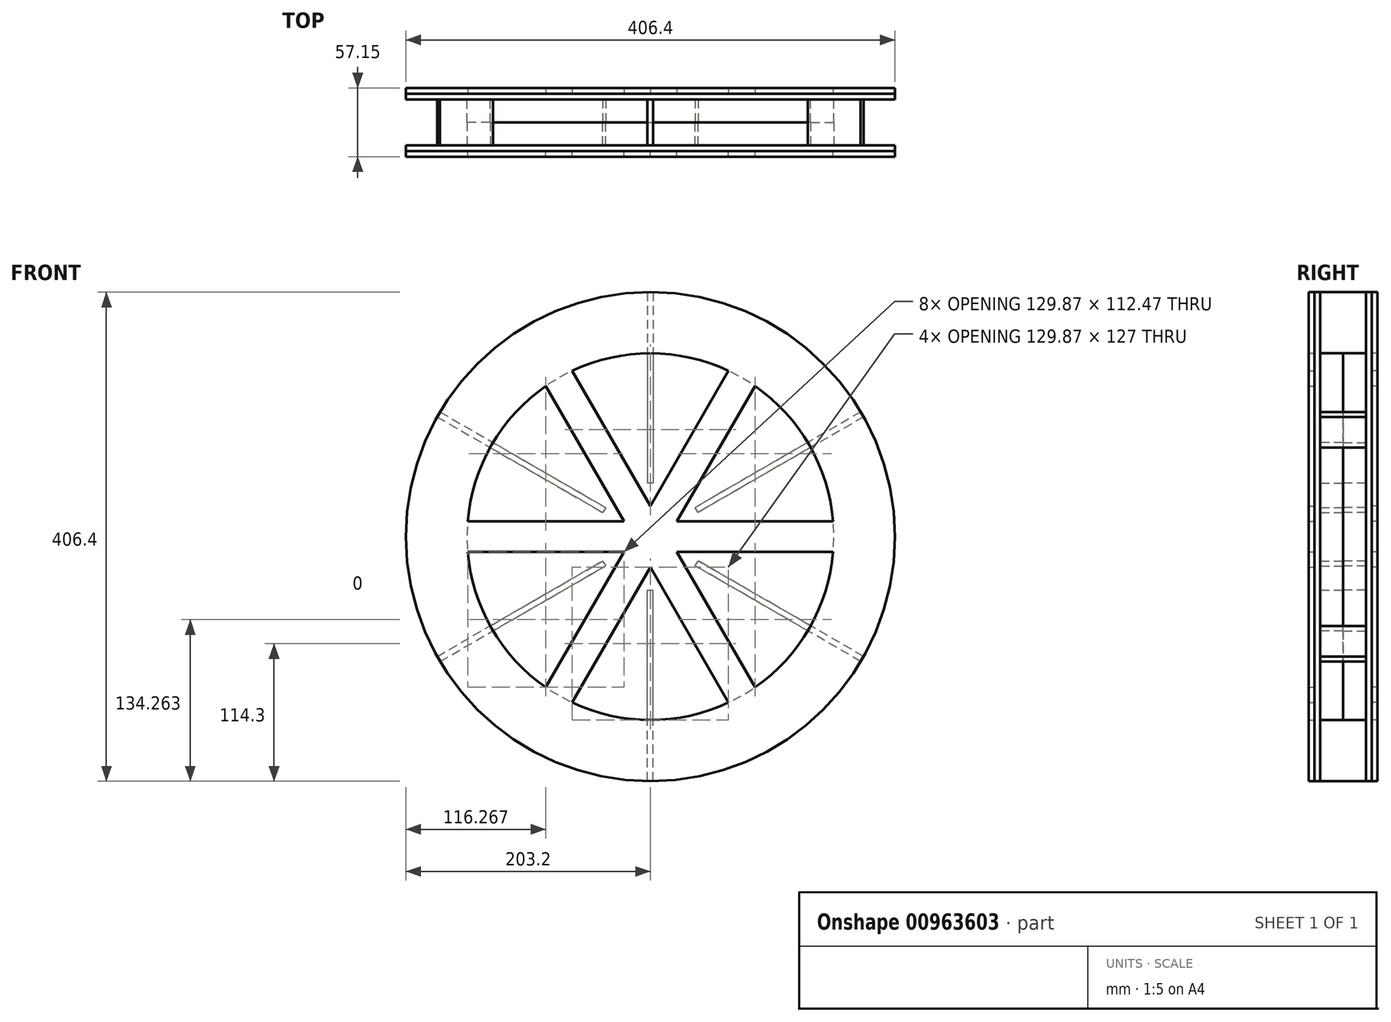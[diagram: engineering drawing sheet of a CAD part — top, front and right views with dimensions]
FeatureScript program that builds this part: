
annotation { "Feature Type Name" : "Feature", "Feature Type Description" : "" }
export const myFeature = defineFeature(function(context is Context, id is Id, definition is map)
    precondition{}
    {
        {
            var Q0;
            Q0=qCreatedBy(makeId("Front.planeOp"),FACE);
            var sketch = newSketch(context, id + "F0", { "sketchPlane" : qUnion([Q0])});
            skCircle(sketch, "E0", {"center": v(0, 0) * mm, "radius": 203.2 * mm});
            skArc(sketch, "E1", {"start": v(-151.87, -12.7) * mm, "mid": v(-131.98, -76.2) * mm, "end": v(-86.93, -125.17) * mm});
            skLineSegment(sketch, "E2.bottom", {"start": v(151.87, 12.7) * mm, "end": v(22, 12.7) * mm});
            skLineSegment(sketch, "E2.top", {"start": v(151.87, -12.7) * mm, "end": v(22, -12.7) * mm});
            skLineSegment(sketch, "E3.left", {"start": v(86.93, 125.17) * mm, "end": v(22, 12.7) * mm});
            skLineSegment(sketch, "E3.right", {"start": v(64.94, 137.87) * mm, "end": v(0, 25.4) * mm});
            skLineSegment(sketch, "E4", {"start": v(0, 0) * mm, "end": v(0, 203.2) * mm, "construction": true});
            skLineSegment(sketch, "E5.MirrorCS", {"start": v(-64.94, 137.87) * mm, "end": v(0, 25.4) * mm});
            skLineSegment(sketch, "E6.MirrorCS", {"start": v(-86.93, 125.17) * mm, "end": v(-22, 12.7) * mm});
            skArc(sketch, "E7.trimOffspring", {"start": v(-86.93, 125.17) * mm, "mid": v(-131.98, 76.2) * mm, "end": v(-151.87, 12.7) * mm});
            skArc(sketch, "E8.trimOffspring", {"start": v(64.94, 137.87) * mm, "mid": v(0, 152.4) * mm, "end": v(-64.94, 137.87) * mm});
            skArc(sketch, "E9.trimOffspring", {"start": v(151.87, 12.7) * mm, "mid": v(131.98, 76.2) * mm, "end": v(86.93, 125.17) * mm});
            skArc(sketch, "E10.trimOffspring", {"start": v(86.93, -125.17) * mm, "mid": v(131.98, -76.2) * mm, "end": v(151.87, -12.7) * mm});
            skArc(sketch, "E11.trimOffspring", {"start": v(-64.94, -137.87) * mm, "mid": v(0, -152.4) * mm, "end": v(64.94, -137.87) * mm});
            skLineSegment(sketch, "E12.trimOffspring", {"start": v(-22, -12.7) * mm, "end": v(-86.93, -125.17) * mm});
            skLineSegment(sketch, "E13.trimOffspring", {"start": v(-22, 12.7) * mm, "end": v(-151.87, 12.7) * mm});
            skLineSegment(sketch, "E14.trimOffspring", {"start": v(0, -25.4) * mm, "end": v(64.94, -137.87) * mm});
            skLineSegment(sketch, "E15.trimOffspring", {"start": v(-22, -12.7) * mm, "end": v(-151.87, -12.7) * mm});
            skLineSegment(sketch, "E16.trimOffspring", {"start": v(22, -12.7) * mm, "end": v(86.93, -125.17) * mm});
            skLineSegment(sketch, "E17.trimOffspring", {"start": v(0, -25.4) * mm, "end": v(-64.94, -137.87) * mm});
            skLineSegment(sketch, "E18", {"start": v(22, 12.7) * mm, "end": v(22, -12.7) * mm, "construction": true});
            skLineSegment(sketch, "E19", {"start": v(22, 12.7) * mm, "end": v(0, 25.4) * mm, "construction": true});
            skLineSegment(sketch, "E20", {"start": v(-22, 12.7) * mm, "end": v(0, 25.4) * mm, "construction": true});
            skSolve(sketch);
        }
        {
            var Q0;
            Q0 = qSketchRegion(id + "F0", true);
            extrude(context, id + "F1", {"entities" : qUnion([Q0]), "depth" : 4.76 * mm, "offsetDistance" : 25.4 * mm});
        }
        {
            var Q0;
            Q0=makeQuery(id+"F1.opExtrude","CAP_FACE",FACE,{"disambiguationData":[OSD([sQuery(id+"F0.wireOp",EDGE,"E0"),sQuery(id+"F0.wireOp",EDGE,"E1"),sQuery(id+"F0.wireOp",EDGE,"E2.bottom"),sQuery(id+"F0.wireOp",EDGE,"E2.top"),sQuery(id+"F0.wireOp",EDGE,"E3.left"),sQuery(id+"F0.wireOp",EDGE,"E3.right"),sQuery(id+"F0.wireOp",EDGE,"E5.MirrorCS"),sQuery(id+"F0.wireOp",EDGE,"E6.MirrorCS"),sQuery(id+"F0.wireOp",EDGE,"E7.trimOffspring"),sQuery(id+"F0.wireOp",EDGE,"E8.trimOffspring"),sQuery(id+"F0.wireOp",EDGE,"E9.trimOffspring"),sQuery(id+"F0.wireOp",EDGE,"E10.trimOffspring"),sQuery(id+"F0.wireOp",EDGE,"E11.trimOffspring"),sQuery(id+"F0.wireOp",EDGE,"E12.trimOffspring"),sQuery(id+"F0.wireOp",EDGE,"E13.trimOffspring"),sQuery(id+"F0.wireOp",EDGE,"E14.trimOffspring"),sQuery(id+"F0.wireOp",EDGE,"E15.trimOffspring"),sQuery(id+"F0.wireOp",EDGE,"E16.trimOffspring"),sQuery(id+"F0.wireOp",EDGE,"E17.trimOffspring")])],"isStart":true});
            var sketch = newSketch(context, id + "F2", { "sketchPlane" : qUnion([Q0])});
            skCircle(sketch, "E21.0", {"center": v(0, 0) * mm, "radius": 203.2 * mm});
            skSolve(sketch);
        }
        {
            var Q0;
            Q0 = qSketchRegion(id + "F2", true);
            extrude(context, id + "F3", {"entities" : qUnion([Q0]), "depth" : 4.76 * mm, "offsetDistance" : 25.4 * mm});
        }
        {
            var Q0;
            Q0=makeQuery(id+"F3.opExtrude","CAP_FACE",FACE,{"disambiguationData":[OSD([sQuery(id+"F2.wireOp",EDGE,"E21.0")])],"isStart":false});
            var sketch = newSketch(context, id + "F4", { "sketchPlane" : qUnion([Q0])});
            skCircle(sketch, "E22", {"center": v(0, 0) * mm, "radius": 152.4 * mm});
            skSolve(sketch);
        }
        {
            var Q0;
            Q0 = qSketchRegion(id + "F4", true);
            extrude(context, id + "F5", {"entities" : qUnion([Q0]), "depth" : 19.05 * mm, "offsetDistance" : 25.4 * mm});
        }
        {
            var Q0;
            Q0=makeQuery(id+"F5.opExtrude","CAP_FACE",FACE,{"disambiguationData":[OSD([sQuery(id+"F4.wireOp",EDGE,"E22")])],"isStart":false});
            var sketch = newSketch(context, id + "F6", { "sketchPlane" : qUnion([Q0])});
            skCircle(sketch, "E23.0", {"center": v(0, 0) * mm, "radius": 203.2 * mm, "construction": true});
            skLineSegment(sketch, "E24.bottom", {"start": v(-2.38, 203.19) * mm, "end": v(2.38, 203.19) * mm});
            skLineSegment(sketch, "E24.top", {"start": v(-2.38, 44.43) * mm, "end": v(2.38, 44.43) * mm});
            skLineSegment(sketch, "E24.left", {"start": v(-2.38, 203.19) * mm, "end": v(-2.38, 44.43) * mm});
            skLineSegment(sketch, "E24.right", {"start": v(2.38, 203.19) * mm, "end": v(2.38, 44.43) * mm});
            skPoint(sketch, "E25", {"position": v(2.38, 152.38) * mm});
            skLineSegment(sketch, "E26.1.0", {"start": v(-174.77, 103.66) * mm, "end": v(-37.29, 24.28) * mm});
            skLineSegment(sketch, "E26.1.1", {"start": v(-177.15, 99.53) * mm, "end": v(-39.67, 20.15) * mm});
            skPoint(sketch, "E26.1.2", {"position": v(-130.78, 78.25) * mm});
            skLineSegment(sketch, "E26.1.3", {"start": v(-39.67, 20.15) * mm, "end": v(-37.29, 24.28) * mm});
            skLineSegment(sketch, "E26.1.4", {"start": v(-177.15, 99.53) * mm, "end": v(-174.77, 103.66) * mm});
            skLineSegment(sketch, "E26.2.0", {"start": v(-177.15, -99.53) * mm, "end": v(-39.67, -20.15) * mm});
            skLineSegment(sketch, "E26.2.1", {"start": v(-174.77, -103.66) * mm, "end": v(-37.29, -24.28) * mm});
            skPoint(sketch, "E26.2.2", {"position": v(-133.16, -74.13) * mm});
            skLineSegment(sketch, "E26.2.3", {"start": v(-37.29, -24.28) * mm, "end": v(-39.67, -20.15) * mm});
            skLineSegment(sketch, "E26.2.4", {"start": v(-174.77, -103.66) * mm, "end": v(-177.15, -99.53) * mm});
            skLineSegment(sketch, "E26.3.0", {"start": v(-2.38, -203.19) * mm, "end": v(-2.38, -44.43) * mm});
            skLineSegment(sketch, "E26.3.1", {"start": v(2.38, -203.19) * mm, "end": v(2.38, -44.43) * mm});
            skPoint(sketch, "E26.3.2", {"position": v(-2.38, -152.38) * mm});
            skLineSegment(sketch, "E26.3.3", {"start": v(2.38, -44.43) * mm, "end": v(-2.38, -44.43) * mm});
            skLineSegment(sketch, "E26.3.4", {"start": v(2.38, -203.19) * mm, "end": v(-2.38, -203.19) * mm});
            skLineSegment(sketch, "E26.4.0", {"start": v(174.77, -103.66) * mm, "end": v(37.29, -24.28) * mm});
            skLineSegment(sketch, "E26.4.1", {"start": v(177.15, -99.53) * mm, "end": v(39.67, -20.15) * mm});
            skPoint(sketch, "E26.4.2", {"position": v(130.78, -78.25) * mm});
            skLineSegment(sketch, "E26.4.3", {"start": v(39.67, -20.15) * mm, "end": v(37.29, -24.28) * mm});
            skLineSegment(sketch, "E26.4.4", {"start": v(177.15, -99.53) * mm, "end": v(174.77, -103.66) * mm});
            skLineSegment(sketch, "E26.5.0", {"start": v(177.15, 99.53) * mm, "end": v(39.67, 20.15) * mm});
            skLineSegment(sketch, "E26.5.1", {"start": v(174.77, 103.66) * mm, "end": v(37.29, 24.28) * mm});
            skPoint(sketch, "E26.5.2", {"position": v(133.16, 74.13) * mm});
            skLineSegment(sketch, "E26.5.3", {"start": v(37.29, 24.28) * mm, "end": v(39.67, 20.15) * mm});
            skLineSegment(sketch, "E26.5.4", {"start": v(174.77, 103.66) * mm, "end": v(177.15, 99.53) * mm});
            skSolve(sketch);
        }
        {
            var Q0;
            Q0 = qSketchRegion(id + "F6", true);
            var Q1;
            Q1=makeQuery(id+"F3.opExtrude","CAP_FACE",FACE,{"disambiguationData":[OSD([sQuery(id+"F2.wireOp",EDGE,"E21.0")])],"isStart":false});
            extrude(context, id + "F7", {"entities" : qUnion([Q0]), "operationType" : NewBodyOperationType.REMOVE, "endBound" : BoundingType.UP_TO_SURFACE, "oppositeDirection" : true, "depth" : 25.4 * mm, "endBoundEntityFace" : qUnion([Q1]), "offsetDistance" : 25.4 * mm});
        }
        {
            var Q0;
            Q0=makeQuery(id+"F5.opExtrude","CAP_FACE",FACE,{"disambiguationData":[OSD([sQuery(id+"F4.wireOp",EDGE,"E22")])],"isStart":false});
            cPlane(context, id + "F8", {"entities" : qUnion([Q0]), "cplaneType" : CPlaneType.OFFSET, "offset" : 0 * mm, "width" : 152.4 * mm, "height" : 152.4 * mm});
        }
        {
            var Q0;
            Q0=makeQuery(id+"F5.opExtrude","SWEPT_BODY",BODY,{"disambiguationData":[OSD([sQuery(id+"F4.wireOp",EDGE,"E22")])]});
            var Q1;
            Q1=makeQuery(id+"F3.opExtrude","SWEPT_BODY",BODY,{"disambiguationData":[OSD([sQuery(id+"F2.wireOp",EDGE,"E21.0")])]});
            var Q2;
            Q2=makeQuery(id+"F1.opExtrude","SWEPT_BODY",BODY,{"disambiguationData":[OSD([sQuery(id+"F0.wireOp",EDGE,"E0"),sQuery(id+"F0.wireOp",EDGE,"E1"),sQuery(id+"F0.wireOp",EDGE,"E2.bottom"),sQuery(id+"F0.wireOp",EDGE,"E2.top"),sQuery(id+"F0.wireOp",EDGE,"E3.left"),sQuery(id+"F0.wireOp",EDGE,"E3.right"),sQuery(id+"F0.wireOp",EDGE,"E5.MirrorCS"),sQuery(id+"F0.wireOp",EDGE,"E6.MirrorCS"),sQuery(id+"F0.wireOp",EDGE,"E7.trimOffspring"),sQuery(id+"F0.wireOp",EDGE,"E8.trimOffspring"),sQuery(id+"F0.wireOp",EDGE,"E9.trimOffspring"),sQuery(id+"F0.wireOp",EDGE,"E10.trimOffspring"),sQuery(id+"F0.wireOp",EDGE,"E11.trimOffspring"),sQuery(id+"F0.wireOp",EDGE,"E12.trimOffspring"),sQuery(id+"F0.wireOp",EDGE,"E13.trimOffspring"),sQuery(id+"F0.wireOp",EDGE,"E14.trimOffspring"),sQuery(id+"F0.wireOp",EDGE,"E15.trimOffspring"),sQuery(id+"F0.wireOp",EDGE,"E16.trimOffspring"),sQuery(id+"F0.wireOp",EDGE,"E17.trimOffspring")])]});
            var Q3;
            Q3=qCreatedBy(id+"F8.planeOp",FACE);
            mirror(context, id + "F9", {"entities" : qUnion([Q0, Q1, Q2]), "mirrorPlane" : qUnion([Q3])});
        }
        {
            var Q0;
            Q0 = qSketchRegion(id + "F6", true);
            extrude(context, id + "F10", {"entities" : qUnion([Q0]), "oppositeDirection" : true, "depth" : 19.05 * mm, "offsetDistance" : 25.4 * mm, "hasSecondDirection" : true, "secondDirectionOppositeDirection" : false, "secondDirectionDepth" : 19.05 * mm});
        }
    });
